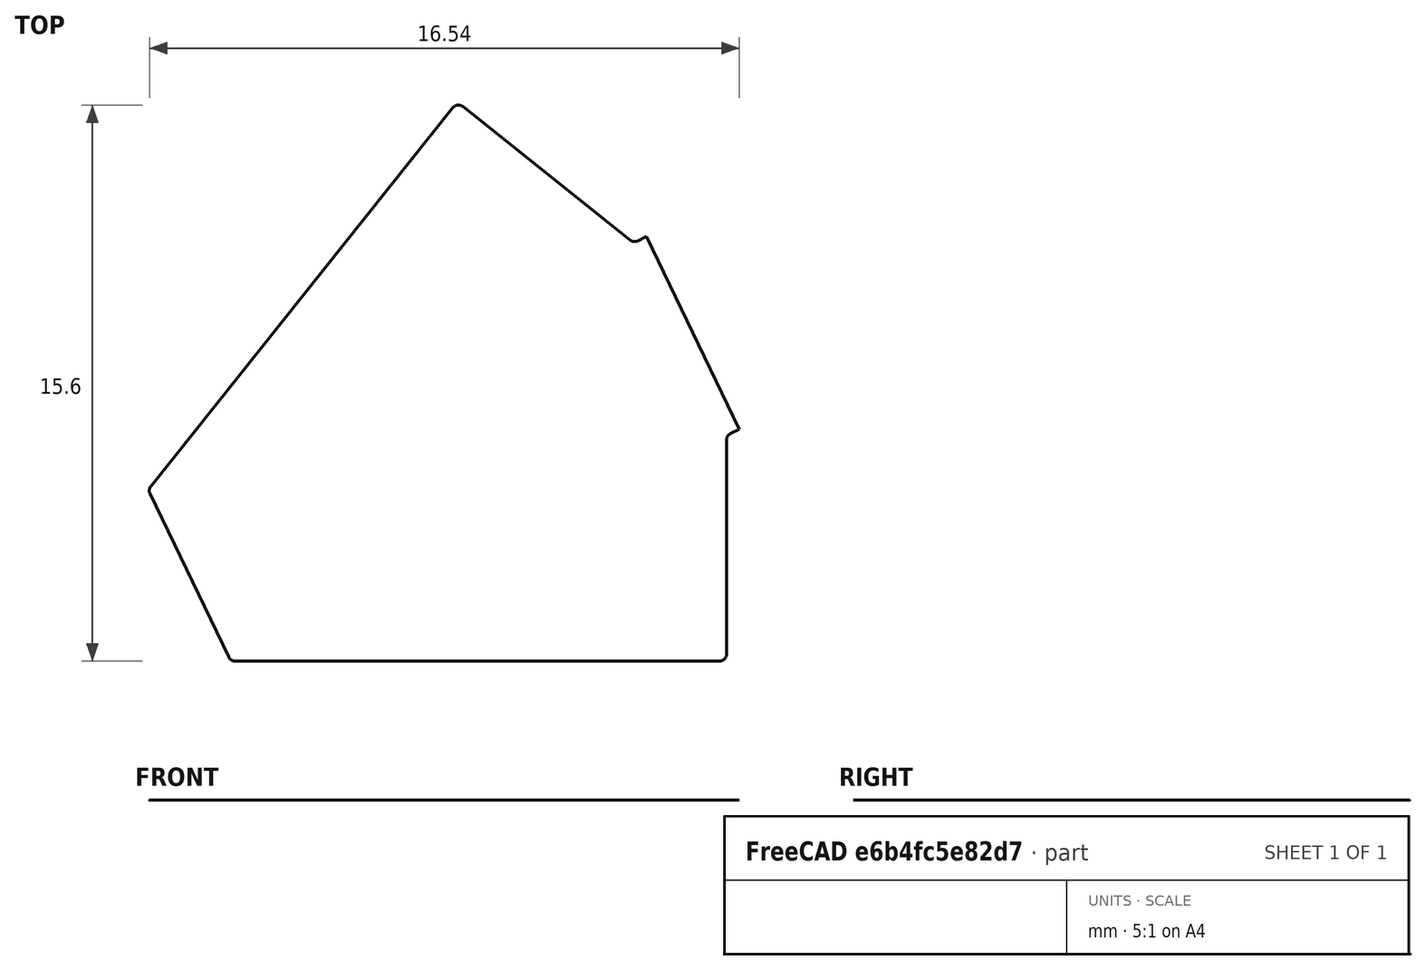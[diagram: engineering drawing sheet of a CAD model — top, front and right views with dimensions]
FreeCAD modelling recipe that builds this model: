
FCSTD DOCUMENT  (FreeCAD 0.18R4 (GitTag))
Label: stator1
License: All rights reserved
LicenseURL: http://en.wikipedia.org/wiki/All_rights_reserved
objects: Sketcher::SketchObject×3, PartDesign::Body×2, Spreadsheet::Sheet×1, Surface::Filling×1
note: 6 computed .brp shape members not serialized (recipe doc carries the construction recipe); baked Part::Feature solids carry a one-line shape summary decoded from their .brp

FEATURE [Spreadsheet::Sheet] Spreadsheet  label="Variables"
  cells = A2=slotNumber; B2(slotNumber)=7; A3=outerDiameter; B3(outerDiameter)=50.15; A4=innerDiameter; B4(innerDiameter)=10; A5=stackLength; B5(stackLength)=20; A6=stackingFactor; B6(stackingFactor)=0.95; A7=cuttingThickness; B7(cuttingThickness)=0.1; A8=skewAngle; B8(skewAngle)=0; A9=segmentAngle; B9(segmentAngle)==360 / slotNumber; A10=tipHeightReduction; B10(tipHeightReduction)=50; A11=toothThickness; B11(toothThickness)=3; A12=yokeThickness; B12(yokeThickness)=4; A13=tipHeight; B13(tipHeight)=0.8; A14=tipAngle; B14(tipAngle)=90; A15=openingLeft; B15(openingLeft)=3; A16=openingRight; B16(openingRight)=3; A17=slotIsolation; B17(slotIsolation)=0.5; A18=windingAngle; B18(windingAngle)=35; A19=heightRatio; B19(heightRatio)=45; A20=roundingRadii; B20(roundingRadii)=0.2
FEATURE [Sketcher::SketchObject] Sketch003  label="StatorSegment"
  MapMode = 5
  Support = -> [XY_Plane]
  expr: Constraints[82] = Variables.roundingRadii
  expr: Constraints[93] = Variables.tipHeight
  expr: Constraints[54] = Variables.innerDiameter / 2 + Variables.yokeThickness
  expr: Constraints[79] = Variables.roundingRadii
  expr: Constraints[21] = 90
  expr: Constraints[64] = Variables.roundingRadii
  expr: Constraints[76] = Variables.roundingRadii
  expr: Constraints[7] = Variables.tipHeight
  expr: Constraints[13] = Variables.innerDiameter / 2
  expr: Constraints[42] = Variables.tipAngle
  expr: Constraints[27] = 90
  expr: Constraints[14] = Variables.segmentAngle / 2
  expr: Constraints[22] = Variables.openingLeft
  expr: Constraints[41] = Variables.tipAngle
  expr: Constraints[4] = Variables.tipHeight * (1 - Variables.tipHeightReduction / 100)
  expr: Constraints[32] = Variables.openingRight
  expr: Constraints[71] = Variables.roundingRadii
  expr: Constraints[46] = Variables.toothThickness / 2
  expr: Constraints[34] = Variables.tipHeight * (1 - Variables.tipHeightReduction / 100)
  expr: Constraints[18] = Variables.outerDiameter / 2
  expr: Constraints[0] = Variables.segmentAngle
  sketch-geometry (36):
    g0: LineSegment [constr] StartX=0 StartY=0 StartZ=0 EndX=15.634 EndY=19.6044 EndZ=0
    g1: LineSegment [constr] StartX=0 StartY=0 StartZ=0 EndX=25.075 EndY=0 EndZ=0
    g2: LineSegment [constr] StartX=0 StartY=0 StartZ=0 EndX=22.5918 EndY=10.8796 EndZ=0
    g3: LineSegment [constr] StartX=8.5045 StartY=23.7788 StartZ=0 EndX=21.2901 EndY=13.5825 EndZ=0
    g4: LineSegment [constr] StartX=21.2901 StartY=13.5825 StartZ=0 EndX=20.6826 EndY=13.29 EndZ=0
    g5: LineSegment [constr] StartX=20.5694 StartY=13.2354 StartZ=0 EndX=20.9298 EndY=13.409 EndZ=0
    g6: ArcOfCircle CenterX=2.20373 CenterY=2.76339 CenterZ=0 NormalX=0 NormalY=0 NormalZ=1 AngleXU=0 Radius=21.5405 StartAngle=0.51693 EndAngle=0.897598
    g7: LineSegment StartX=15.634 StartY=19.6044 StartZ=0 EndX=3.11745 EndY=3.90916 EndZ=0
    g8: ArcOfCircle CenterX=0 CenterY=0 CenterZ=0 NormalX=0 NormalY=0 NormalZ=1 AngleXU=0 Radius=5 StartAngle=0 EndAngle=0.897598
    g9: LineSegment [constr] StartX=22.5918 StartY=10.8796 StartZ=0 EndX=21.2901 EndY=13.5825 EndZ=0
    g10: LineSegment [constr] StartX=23.8934 StartY=8.17673 StartZ=0 EndX=23.2859 EndY=7.88415 EndZ=0
    g11: LineSegment [constr] StartX=22.5918 StartY=10.8796 StartZ=0 EndX=23.8934 EndY=8.17673 EndZ=0
    g12: LineSegment [constr] StartX=23.1727 StartY=7.82962 StartZ=0 EndX=23.5331 EndY=8.00317 EndZ=0
    g13: ArcOfCircle CenterX=3.5345 CenterY=0 CenterZ=0 NormalX=0 NormalY=0 NormalZ=1 AngleXU=0 Radius=21.5405 StartAngle=0 EndAngle=0.380668
    g14: LineSegment StartX=5 StartY=0 StartZ=0 EndX=25.075 EndY=0 EndZ=0
    g15: LineSegment StartX=20.4711 StartY=13.3138 StartZ=0 EndX=15.777 EndY=17.0572 EndZ=0
    g16: LineSegment StartX=15.496 StartY=17.0255 StartZ=0 EndX=7.02891 EndY=6.40816 EndZ=0
    g17: LineSegment StartX=7.00508 StartY=6.19668 StartZ=0 EndX=9.21236 EndY=1.61322 EndZ=0
    g18: LineSegment StartX=9.39255 StartY=1.5 StartZ=0 EndX=22.9727 EndY=1.5 EndZ=0
    g19: LineSegment StartX=23.1727 StartY=1.7 StartZ=0 EndX=23.1727 EndY=7.70395 EndZ=0
    g20: LineSegment [constr] StartX=7.02891 StartY=6.40816 StartZ=0 EndX=5.85616 EndY=7.34339 EndZ=0
    g21: LineSegment [constr] StartX=9.39255 StartY=1.5 StartZ=0 EndX=9.39255 EndY=0 EndZ=0
    g22: LineSegment [constr] StartX=0 StartY=0 StartZ=0 EndX=8.10872 EndY=3.90495 EndZ=0
    g23: LineSegment [constr] StartX=20.5694 StartY=13.2354 StartZ=0 EndX=20.9298 EndY=13.409 EndZ=0
    g24: LineSegment [constr] StartX=23.1727 StartY=7.82962 StartZ=0 EndX=23.5331 EndY=8.00317 EndZ=0
    g25: ArcOfCircle CenterX=20.5958 CenterY=13.4702 CenterZ=0 NormalX=0 NormalY=0 NormalZ=1 AngleXU=0 Radius=0.2 StartAngle=4.03919 EndAngle=5.16119
    g26: LineSegment [constr] StartX=20.4711 StartY=13.3138 StartZ=0 EndX=20.5694 EndY=13.2354 EndZ=0
    g27: ArcOfCircle CenterX=15.6523 CenterY=16.9008 CenterZ=0 NormalX=0 NormalY=0 NormalZ=1 AngleXU=0 Radius=0.2 StartAngle=0.897598 EndAngle=2.46839
    g28: ArcOfCircle CenterX=7.18527 CenterY=6.28346 CenterZ=0 NormalX=0 NormalY=0 NormalZ=1 AngleXU=0 Radius=0.2 StartAngle=2.46839 EndAngle=3.59039
    g29: ArcOfCircle CenterX=9.39255 CenterY=1.7 CenterZ=0 NormalX=0 NormalY=0 NormalZ=1 AngleXU=0 Radius=0.2 StartAngle=3.59039 EndAngle=4.71239
    g30: ArcOfCircle CenterX=22.9727 CenterY=1.7 CenterZ=0 NormalX=0 NormalY=0 NormalZ=1 AngleXU=0 Radius=0.2 StartAngle=4.71239 EndAngle=6.28319
    g31: ArcOfCircle CenterX=23.3727 CenterY=7.70395 CenterZ=0 NormalX=0 NormalY=0 NormalZ=1 AngleXU=0 Radius=0.2 StartAngle=2.0196 EndAngle=3.14159
    g32: LineSegment [constr] StartX=23.2859 StartY=7.88415 StartZ=0 EndX=23.1727 EndY=7.82962 EndZ=0
    g33: LineSegment [constr] StartX=23.1727 StartY=7.82962 StartZ=0 EndX=23.1727 EndY=7.70395 EndZ=0
    g34: LineSegment StartX=20.9298 StartY=13.409 StartZ=0 EndX=20.6826 EndY=13.29 EndZ=0
    g35: LineSegment StartX=23.2859 StartY=7.88415 StartZ=0 EndX=23.5331 EndY=8.00317 EndZ=0
  constraints (94):
    c: Angle(g1,g0) = 0.897598
    c: Symmetric(g3,g3,g0)
    c: Coincident(g4,g3)
    c: PointOnObject(g5,g4)
    c: Distance(g5) = 0.4
    c: Coincident(g6,g5)
    c: PointOnObject(g6,g0)
    c: Distance(g5,g3) = 0.8
    c: Coincident(g7,g6)
    c: PointOnObject(g7,g0)
    c: PointOnObject(g8,g1)
    c: Coincident(g8,g-1)
    c: Coincident(g8,g7)
    c: Radius(g8) = 5
    c: Angle(g-1,g2) = 0.448799
    c: Angle(g-1,g1) = 0
    c: Coincident(g2,g8)
    c: Coincident(g0,g8)
    c: Distance(g2) = 25.075
    c: Coincident(g9,g2)
    c: Coincident(g9,g3)
    c: Angle(g9,g2) = 1.5708
    c: Distance(g9) = 3
    c: Coincident(g6,g0)
    c: Equal(g0,g2)
    c: Equal(g1,g2)
    c: Coincident(g1,g8)
    c: Angle(g4,g9) = 1.5708
    c: Coincident(g11,g2)
    c: Coincident(g11,g10)
    c: Angle(g2,g11) = 1.5708
    c: Angle(g11,g10) = 1.5708
    c: Distance(g11) = 3
    c: Angle(g10,g12) = 0
    c: Distance(g12,g12) = 0.4
    c: PointOnObject(g13,g1)
    c: Coincident(g13,g12)
    c: Coincident(g13,g1)
    c: Coincident(g14,g8)
    c: Coincident(g14,g13)
    c: Horizontal(g18)
    c: Angle(g16,g15) = 1.5708
    c: Angle(g19,g18) = 1.5708
    c: PointOnObject(g20,g7)
    c: Angle(g16,g20) = 1.5708
    c: Angle(g20,g0) = 1.5708
    c: Distance(g20) = 1.5
    c: PointOnObject(g21,g14)
    c: Angle(g21,g18) = 1.5708
    c: Equal(g21,g20)
    c: Coincident(g22,g8)
    c: PointOnObject(g22,g17)
    c: Angle(g17,g22) = 1.5708
    c: PointOnObject(g22,g2)
    c: Distance(g8,g22) = 9
    c: Coincident(g23,g5)
    c: Coincident(g23,g6)
    c: Coincident(g24,g12)
    c: Coincident(g24,g13)
    c: Tangent(g4,g25) = 1.5708
    c: Tangent(g15,g25) = 1.5708
    c: Coincident(g26,g15)
    c: Coincident(g26,g5)
    c: Parallel(g26,g15)
    c: Radius(g25) = 0.2
    c: PointOnObject(g4,g5)
    c: Tangent(g16,g27) = -1.5708
    c: Tangent(g15,g27) = -1.5708
    c: Equal(g27,g25)
    c: Tangent(g17,g28) = -1.5708
    c: Tangent(g16,g28) = -1.5708
    c: Radius(g28) = 0.2
    c: Coincident(g20,g16)
    c: Tangent(g17,g29) = -1.5708
    c: Tangent(g18,g29) = -1.5708
    c: Coincident(g21,g18)
    c: Radius(g29) = 0.2
    c: Tangent(g18,g30) = -1.5708
    c: Tangent(g19,g30) = -1.5708
    c: Radius(g30) = 0.2
    c: Tangent(g19,g31) = 1.5708
    c: Tangent(g10,g31) = -1.5708
    c: Radius(g31) = 0.2
    c: Coincident(g32,g10)
    c: Coincident(g33,g32)
    c: Coincident(g33,g19)
    c: Parallel(g19,g33)
    c: Parallel(g32,g10)
    c: Coincident(g12,g32)
    c: Coincident(g34,g6)
    c: Coincident(g34,g4)
    c: Coincident(g35,g31)
    c: Coincident(g35,g13)
    c: Distance(g12,g10) = 0.8
FEATURE [Sketcher::SketchObject] Sketch  label="StatorStack"
  MapMode = 5
  Support = -> [XY_Plane001]
  expr: Constraints[20] = Variables.innerDiameter / 2
  expr: Constraints[10] = Variables.outerDiameter / 2
  expr: Constraints[9] = Variables.innerDiameter / 2
  expr: Constraints[8] = Variables.stackLength
  sketch-geometry (8):
    g0: LineSegment StartX=-10 StartY=5 StartZ=0 EndX=10 EndY=5 EndZ=0
    g1: LineSegment StartX=10 StartY=5 StartZ=0 EndX=10 EndY=25.075 EndZ=0
    g2: LineSegment StartX=10 StartY=25.075 StartZ=0 EndX=-10 EndY=25.075 EndZ=0
    g3: LineSegment StartX=-10 StartY=25.075 StartZ=0 EndX=-10 EndY=5 EndZ=0
    g4: LineSegment StartX=-10 StartY=-5 StartZ=0 EndX=10 EndY=-5 EndZ=0
    g5: LineSegment StartX=10 StartY=-5 StartZ=0 EndX=10 EndY=-25.075 EndZ=0
    g6: LineSegment StartX=10 StartY=-25.075 StartZ=0 EndX=-10 EndY=-25.075 EndZ=0
    g7: LineSegment StartX=-10 StartY=-25.075 StartZ=0 EndX=-10 EndY=-5 EndZ=0
  constraints (22):
    c: Coincident(g0,g1)
    c: Coincident(g1,g2)
    c: Coincident(g2,g3)
    c: Coincident(g3,g0)
    c: Horizontal(g2)
    c: Vertical(g1)
    c: Vertical(g3)
    c: Symmetric(g0,g0,g-2)
    c: DistanceX(g0,g0) = 20
    c: DistanceY(g-1,g0) = 5
    c: DistanceY(g-1,g1) = 25.075
    c: Coincident(g4,g5)
    c: Coincident(g5,g6)
    c: Coincident(g6,g7)
    c: Coincident(g7,g4)
    c: Horizontal(g6)
    c: Vertical(g5)
    c: Vertical(g7)
    c: Equal(g4,g0)
    c: Symmetric(g4,g4,g-2)
    c: DistanceY(g4,g-1) = 5
    c: Equal(g7,g3)
FEATURE [PartDesign::Body] Body001  label="SideView"
  Group = -> [Sketch]
  Origin = -> Origin001
FEATURE [Sketcher::SketchObject] Sketch004  label="SlotSketch"
  MapMode = 5
  Support = -> [XY_Plane]
  expr: Constraints[82] = Variables.roundingRadii
  expr: Constraints[54] = Variables.innerDiameter / 2 + Variables.yokeThickness
  expr: Constraints[79] = Variables.roundingRadii
  expr: Constraints[21] = 90
  expr: Constraints[64] = Variables.roundingRadii
  expr: Constraints[76] = Variables.roundingRadii
  expr: Constraints[42] = Variables.tipAngle
  expr: Constraints[13] = Variables.innerDiameter / 2
  expr: Constraints[7] = Variables.tipHeight
  expr: Constraints[27] = 90
  expr: Constraints[41] = Variables.tipAngle
  expr: Constraints[22] = Variables.openingLeft
  expr: Constraints[14] = Variables.segmentAngle / 2
  expr: Constraints[4] = Variables.tipHeight * (1 - Variables.tipHeightReduction / 100)
  expr: Constraints[95] = Variables.tipHeight
  expr: Constraints[32] = Variables.openingRight
  expr: Constraints[71] = Variables.roundingRadii
  expr: Constraints[46] = Variables.toothThickness / 2
  expr: Constraints[0] = Variables.segmentAngle
  expr: Constraints[18] = Variables.outerDiameter / 2
  expr: Constraints[34] = Variables.tipHeight * (1 - Variables.tipHeightReduction / 100)
  sketch-geometry (37):
    g0: LineSegment [constr] StartX=0 StartY=0 StartZ=0 EndX=15.634 EndY=19.6044 EndZ=0
    g1: LineSegment [constr] StartX=0 StartY=0 StartZ=0 EndX=25.075 EndY=0 EndZ=0
    g2: LineSegment [constr] StartX=0 StartY=0 StartZ=0 EndX=22.5918 EndY=10.8796 EndZ=0
    g3: LineSegment [constr] StartX=8.5045 StartY=23.7788 StartZ=0 EndX=21.2901 EndY=13.5825 EndZ=0
    g4: LineSegment [constr] StartX=21.2901 StartY=13.5825 StartZ=0 EndX=20.6826 EndY=13.29 EndZ=0
    g5: LineSegment [constr] StartX=20.5694 StartY=13.2354 StartZ=0 EndX=20.9298 EndY=13.409 EndZ=0
    g6: ArcOfCircle [constr] CenterX=2.20373 CenterY=2.76339 CenterZ=0 NormalX=0 NormalY=0 NormalZ=1 AngleXU=0 Radius=21.5405 StartAngle=0.51693 EndAngle=0.897598
    g7: LineSegment [constr] StartX=15.634 StartY=19.6044 StartZ=0 EndX=3.11745 EndY=3.90916 EndZ=0
    g8: ArcOfCircle [constr] CenterX=0 CenterY=0 CenterZ=0 NormalX=0 NormalY=0 NormalZ=1 AngleXU=0 Radius=5 StartAngle=0 EndAngle=0.897598
    g9: LineSegment [constr] StartX=22.5918 StartY=10.8796 StartZ=0 EndX=21.2901 EndY=13.5825 EndZ=0
    g10: LineSegment [constr] StartX=23.8934 StartY=8.17673 StartZ=0 EndX=23.2859 EndY=7.88415 EndZ=0
    g11: LineSegment [constr] StartX=22.5918 StartY=10.8796 StartZ=0 EndX=23.8934 EndY=8.17673 EndZ=0
    g12: LineSegment [constr] StartX=23.1727 StartY=7.82962 StartZ=0 EndX=23.5331 EndY=8.00317 EndZ=0
    g13: ArcOfCircle [constr] CenterX=3.5345 CenterY=0 CenterZ=0 NormalX=0 NormalY=0 NormalZ=1 AngleXU=0 Radius=21.5405 StartAngle=0 EndAngle=0.380668
    g14: LineSegment [constr] StartX=5 StartY=0 StartZ=0 EndX=25.075 EndY=0 EndZ=0
    g15: LineSegment StartX=20.4711 StartY=13.3138 StartZ=0 EndX=15.777 EndY=17.0572 EndZ=0
    g16: LineSegment StartX=15.496 StartY=17.0255 StartZ=0 EndX=7.02891 EndY=6.40816 EndZ=0
    g17: LineSegment StartX=7.00508 StartY=6.19668 StartZ=0 EndX=9.21236 EndY=1.61322 EndZ=0
    g18: LineSegment StartX=9.39255 StartY=1.5 StartZ=0 EndX=22.9727 EndY=1.5 EndZ=0
    g19: LineSegment StartX=23.1727 StartY=1.7 StartZ=0 EndX=23.1727 EndY=7.70395 EndZ=0
    g20: LineSegment [constr] StartX=7.02891 StartY=6.40816 StartZ=0 EndX=5.85616 EndY=7.34339 EndZ=0
    g21: LineSegment [constr] StartX=9.39255 StartY=1.5 StartZ=0 EndX=9.39255 EndY=0 EndZ=0
    g22: LineSegment [constr] StartX=0 StartY=0 StartZ=0 EndX=8.10872 EndY=3.90495 EndZ=0
    g23: LineSegment [constr] StartX=20.5694 StartY=13.2354 StartZ=0 EndX=20.9298 EndY=13.409 EndZ=0
    g24: LineSegment [constr] StartX=23.1727 StartY=7.82962 StartZ=0 EndX=23.5331 EndY=8.00317 EndZ=0
    g25: ArcOfCircle CenterX=20.5958 CenterY=13.4702 CenterZ=0 NormalX=0 NormalY=0 NormalZ=1 AngleXU=0 Radius=0.2 StartAngle=4.03919 EndAngle=5.16119
    g26: LineSegment [constr] StartX=20.4711 StartY=13.3138 StartZ=0 EndX=20.5694 EndY=13.2354 EndZ=0
    g27: ArcOfCircle CenterX=15.6523 CenterY=16.9008 CenterZ=0 NormalX=0 NormalY=0 NormalZ=1 AngleXU=0 Radius=0.2 StartAngle=0.897598 EndAngle=2.46839
    g28: ArcOfCircle CenterX=7.18527 CenterY=6.28346 CenterZ=0 NormalX=0 NormalY=0 NormalZ=1 AngleXU=0 Radius=0.2 StartAngle=2.46839 EndAngle=3.59039
    g29: ArcOfCircle CenterX=9.39255 CenterY=1.7 CenterZ=0 NormalX=0 NormalY=0 NormalZ=1 AngleXU=0 Radius=0.2 StartAngle=3.59039 EndAngle=4.71239
    g30: ArcOfCircle CenterX=22.9727 CenterY=1.7 CenterZ=0 NormalX=0 NormalY=0 NormalZ=1 AngleXU=0 Radius=0.2 StartAngle=4.71239 EndAngle=6.28319
    g31: ArcOfCircle CenterX=23.3727 CenterY=7.70395 CenterZ=0 NormalX=0 NormalY=0 NormalZ=1 AngleXU=0 Radius=0.2 StartAngle=2.0196 EndAngle=3.14159
    g32: LineSegment [constr] StartX=23.2859 StartY=7.88415 StartZ=0 EndX=23.1727 EndY=7.82962 EndZ=0
    g33: LineSegment [constr] StartX=23.1727 StartY=7.82962 StartZ=0 EndX=23.1727 EndY=7.70395 EndZ=0
    g34: LineSegment StartX=20.9298 StartY=13.409 StartZ=0 EndX=20.6826 EndY=13.29 EndZ=0
    g35: LineSegment StartX=23.2859 StartY=7.88415 StartZ=0 EndX=23.5331 EndY=8.00317 EndZ=0
    g36: LineSegment StartX=20.9298 StartY=13.409 StartZ=0 EndX=23.5331 EndY=8.00317 EndZ=0
  constraints (96):
    c: Angle(g1,g0) = 0.897598
    c: Symmetric(g3,g3,g0)
    c: Coincident(g4,g3)
    c: PointOnObject(g5,g4)
    c: Distance(g5) = 0.4
    c: Coincident(g6,g5)
    c: PointOnObject(g6,g0)
    c: Distance(g5,g3) = 0.8
    c: Coincident(g7,g6)
    c: PointOnObject(g7,g0)
    c: PointOnObject(g8,g1)
    c: Coincident(g8,g-1)
    c: Coincident(g8,g7)
    c: Radius(g8) = 5
    c: Angle(g-1,g2) = 0.448799
    c: Angle(g-1,g1) = 0
    c: Coincident(g2,g8)
    c: Coincident(g0,g8)
    c: Distance(g2) = 25.075
    c: Coincident(g9,g2)
    c: Coincident(g9,g3)
    c: Angle(g9,g2) = 1.5708
    c: Distance(g9) = 3
    c: Coincident(g6,g0)
    c: Equal(g0,g2)
    c: Equal(g1,g2)
    c: Coincident(g1,g8)
    c: Angle(g4,g9) = 1.5708
    c: Coincident(g11,g2)
    c: Coincident(g11,g10)
    c: Angle(g2,g11) = 1.5708
    c: Angle(g11,g10) = 1.5708
    c: Distance(g11) = 3
    c: Angle(g10,g12) = 0
    c: Distance(g12,g12) = 0.4
    c: PointOnObject(g13,g1)
    c: Coincident(g13,g12)
    c: Coincident(g13,g1)
    c: Coincident(g14,g8)
    c: Coincident(g14,g13)
    c: Horizontal(g18)
    c: Angle(g16,g15) = 1.5708
    c: Angle(g19,g18) = 1.5708
    c: PointOnObject(g20,g7)
    c: Angle(g16,g20) = 1.5708
    c: Angle(g20,g0) = 1.5708
    c: Distance(g20) = 1.5
    c: PointOnObject(g21,g14)
    c: Angle(g21,g18) = 1.5708
    c: Equal(g21,g20)
    c: Coincident(g22,g8)
    c: PointOnObject(g22,g17)
    c: Angle(g17,g22) = 1.5708
    c: PointOnObject(g22,g2)
    c: Distance(g8,g22) = 9
    c: Coincident(g23,g5)
    c: Coincident(g23,g6)
    c: Coincident(g24,g12)
    c: Coincident(g24,g13)
    c: Tangent(g4,g25) = 1.5708
    c: Tangent(g15,g25) = 1.5708
    c: Coincident(g26,g15)
    c: Coincident(g26,g5)
    c: Parallel(g26,g15)
    c: Radius(g25) = 0.2
    c: PointOnObject(g4,g5)
    c: Tangent(g16,g27) = -1.5708
    c: Tangent(g15,g27) = -1.5708
    c: Equal(g27,g25)
    c: Tangent(g17,g28) = -1.5708
    c: Tangent(g16,g28) = -1.5708
    c: Radius(g28) = 0.2
    c: Coincident(g20,g16)
    c: Tangent(g17,g29) = -1.5708
    c: Tangent(g18,g29) = -1.5708
    c: Coincident(g21,g18)
    c: Radius(g29) = 0.2
    c: Tangent(g18,g30) = -1.5708
    c: Tangent(g19,g30) = -1.5708
    c: Radius(g30) = 0.2
    c: Tangent(g19,g31) = 1.5708
    c: Tangent(g10,g31) = -1.5708
    c: Radius(g31) = 0.2
    c: Coincident(g32,g10)
    c: Coincident(g33,g32)
    c: Coincident(g33,g19)
    c: Parallel(g19,g33)
    c: Parallel(g32,g10)
    c: Coincident(g12,g32)
    c: Coincident(g34,g6)
    c: Coincident(g34,g4)
    c: Coincident(g35,g31)
    c: Coincident(g35,g13)
    c: Coincident(g36,g34)
    c: Coincident(g36,g35)
    c: Distance(g12,g10) = 0.8
FEATURE [PartDesign::Body] Body  label="TopView"
  Group = -> [Sketch003,Sketch004]
  Origin = -> Origin
FEATURE [Surface::Filling] Surface  label="Slot"
  Anisotropy = false
  BoundaryEdges = -> [Sketch004]
  BoundaryOrder = [0,0,0,0,0,0,0,0,0,0,0,0,0,0]
  Degree = 3
  Iterations = 2
  MaximumDegree = 8
  MaximumSegments = 9
  PointsOnCurve = 15
  TolAngular = 0.01
  TolCurvature = 0.1
  Tolerance2d = 1e-05
  Tolerance3d = 0.0001
